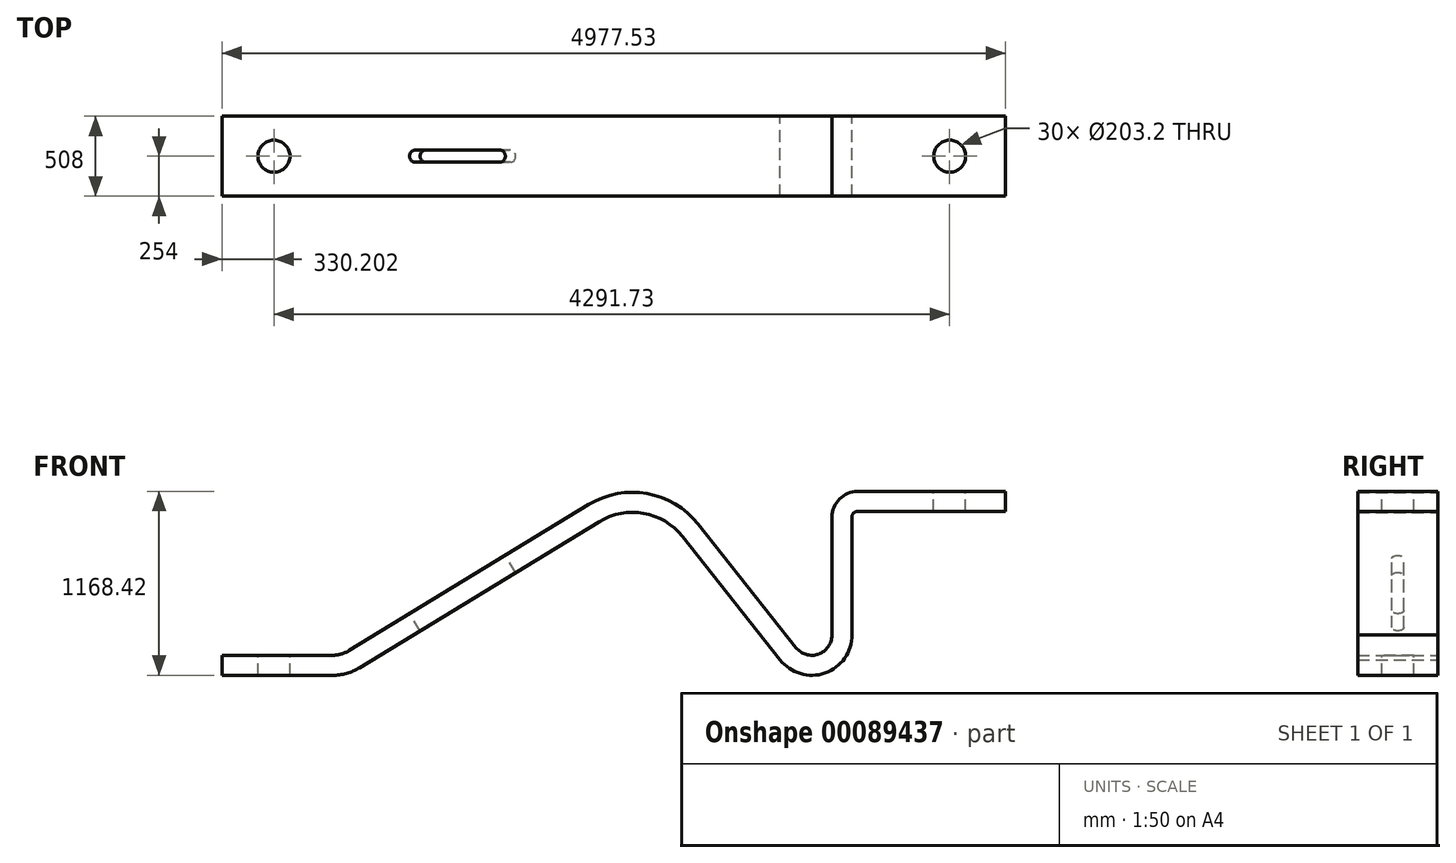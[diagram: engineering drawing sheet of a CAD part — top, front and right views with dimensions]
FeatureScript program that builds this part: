
annotation { "Feature Type Name" : "Feature", "Feature Type Description" : "" }
export const myFeature = defineFeature(function(context is Context, id is Id, definition is map)
    precondition{}
    {
        {
            var Q0;
            Q0=qCreatedBy(makeId("Front.planeOp"),FACE);
            var sketch = newSketch(context, id + "F0", { "sketchPlane" : qUnion([Q0])});
            skLineSegment(sketch, "E0", {"start": v(-1257.48, 129.45) * mm, "end": v(-555.68, 129.45) * mm});
            skLineSegment(sketch, "E1", {"start": v(-1257.48, 256.45) * mm, "end": v(-555.68, 256.45) * mm});
            skPoint(sketch, "E2", {"position": v(-555.68, 459.65) * mm});
            skArc(sketch, "E3", {"start": v(1071.43, 1213.55) * mm, "mid": v(1442.7, 1283.22) * mm, "end": v(1767, 1089.53) * mm});
            skLineSegment(sketch, "E4", {"start": v(-449.9, 286.15) * mm, "end": v(1071.43, 1213.55) * mm});
            skArc(sketch, "E5", {"start": v(1137.54, 1105.1) * mm, "mid": v(1420.4, 1158.2) * mm, "end": v(1667.5, 1010.62) * mm});
            skLineSegment(sketch, "E6", {"start": v(1667.5, 1010.62) * mm, "end": v(2290, 225.63) * mm});
            skArc(sketch, "E7", {"start": v(2389.51, 304.54) * mm, "mid": v(2530.8, 263.52) * mm, "end": v(2616.02, 383.45) * mm});
            skLineSegment(sketch, "E8", {"start": v(2831.05, 1297.85) * mm, "end": v(3720.05, 1297.85) * mm});
            skLineSegment(sketch, "E9", {"start": v(2781.12, 1170.85) * mm, "end": v(3720.05, 1170.85) * mm});
            skLineSegment(sketch, "E10", {"start": v(2831.05, 1297.85) * mm, "end": v(2781.12, 1297.85) * mm});
            skLineSegment(sketch, "E11", {"start": v(2743.02, 387.11) * mm, "end": v(2743.02, 1132.75) * mm});
            skArc(sketch, "E12", {"start": v(2781.12, 1170.85) * mm, "mid": v(2754.18, 1159.7) * mm, "end": v(2743.02, 1132.75) * mm});
            skArc(sketch, "E13", {"start": v(2781.12, 1297.85) * mm, "mid": v(2664.38, 1249.5) * mm, "end": v(2616.02, 1132.75) * mm});
            skLineSegment(sketch, "E14", {"start": v(3720.05, 1297.85) * mm, "end": v(3720.05, 1170.85) * mm});
            skLineSegment(sketch, "E15", {"start": v(-1257.48, 256.45) * mm, "end": v(-1257.48, 129.45) * mm});
            skArc(sketch, "E16", {"start": v(-555.68, 256.45) * mm, "mid": v(-500.75, 264.02) * mm, "end": v(-449.9, 286.15) * mm});
            skArc(sketch, "E17", {"start": v(-555.68, 129.45) * mm, "mid": v(-466.42, 141.74) * mm, "end": v(-383.8, 177.7) * mm});
            skLineSegment(sketch, "E18", {"start": v(2616.02, 1132.75) * mm, "end": v(2616.02, 383.45) * mm});
            skLineSegment(sketch, "E19", {"start": v(1767, 1089.53) * mm, "end": v(2389.51, 304.54) * mm});
            skLineSegment(sketch, "E20", {"start": v(-383.8, 177.7) * mm, "end": v(1137.54, 1105.1) * mm});
            skArc(sketch, "E21", {"start": v(2287.73, 228.5) * mm, "mid": v(2572.6, 143.57) * mm, "end": v(2743.02, 387.11) * mm});
            skSolve(sketch);
        }
        {
            var Q0;
            Q0 = qSketchRegion(id + "F0", true);
            extrude(context, id + "F1", {"entities" : qUnion([Q0]), "endBound" : BoundingType.SYMMETRIC, "depth" : 508 * mm});
        }
        {
            var Q0;
            Q0=makeQuery(id+"F1.opExtrude","SWEPT_FACE",FACE,{"disambiguationData":[OSD([sQuery(id+"F0.wireOp",EDGE,"E1")])]});
            var sketch = newSketch(context, id + "F2", { "sketchPlane" : qUnion([Q0])});
            skLineSegment(sketch, "E22", {"start": v(-1257.48, 0) * mm, "end": v(-927.28, 0) * mm, "construction": true});
            skPoint(sketch, "E22.endSnap0", {"position": v(-1257.48, 0) * mm});
            skCircle(sketch, "E23", {"center": v(-927.28, 0) * mm, "radius": 101.6 * mm});
            skPoint(sketch, "E24.0", {"position": v(3720.05, 0) * mm});
            skLineSegment(sketch, "E25", {"start": v(3720.05, 0) * mm, "end": v(3364.45, 0) * mm, "construction": true});
            skCircle(sketch, "E26", {"center": v(3364.45, 0) * mm, "radius": 101.6 * mm});
            skSolve(sketch);
        }
        {
            var Q0;
            Q0 = qSketchRegion(id + "F2", true);
            extrude(context, id + "F3", {"entities" : qUnion([Q0]), "operationType" : NewBodyOperationType.REMOVE, "endBound" : BoundingType.THROUGH_ALL, "oppositeDirection" : true, "depth" : 25.4 * mm});
        }
        {
            var Q0;
            Q0=makeQuery(id+"F1.opExtrude","SWEPT_FACE",FACE,{"disambiguationData":[OSD([sQuery(id+"F0.wireOp",EDGE,"E8"),sQuery(id+"F0.wireOp",EDGE,"E10")])]});
            var sketch = newSketch(context, id + "F4", { "sketchPlane" : qUnion([Q0])});
            skLineSegment(sketch, "E27", {"start": v(3720.05, 0) * mm, "end": v(3364.45, 0) * mm, "construction": true});
            skPoint(sketch, "E27.endSnap0", {"position": v(3720.05, 0) * mm});
            skCircle(sketch, "E28", {"center": v(3364.45, 0) * mm, "radius": 101.6 * mm});
            skSolve(sketch);
        }
        {
            var Q0;
            Q0 = qSketchRegion(id + "F4", true);
            extrude(context, id + "F5", {"entities" : qUnion([Q0]), "operationType" : NewBodyOperationType.REMOVE, "endBound" : BoundingType.THROUGH_ALL, "oppositeDirection" : true, "depth" : 25.4 * mm});
        }
        {
            var Q0;
            Q0=makeQuery(id+"F1.opExtrude","SWEPT_FACE",FACE,{"disambiguationData":[OSD([sQuery(id+"F0.wireOp",EDGE,"E4")])]});
            var sketch = newSketch(context, id + "F6", { "sketchPlane" : qUnion([Q0])});
            skPoint(sketch, "E29.0", {"position": v(-940.22, 0) * mm});
            skLineSegment(sketch, "E30", {"start": v(-940.22, 0) * mm, "end": v(-884.9, 0) * mm, "construction": true});
            skLineSegment(sketch, "E31", {"start": v(253.58, 38.1) * mm, "end": v(888.58, 38.1) * mm});
            skLineSegment(sketch, "E32", {"start": v(253.58, -38.1) * mm, "end": v(888.58, -38.1) * mm});
            skPoint(sketch, "E33.center.orphan", {"position": v(888.58, 0) * mm});
            skPoint(sketch, "E34.end.orphan", {"position": v(253.58, 0) * mm});
            skArc(sketch, "E35", {"start": v(253.58, 38.1) * mm, "mid": v(215.48, 0) * mm, "end": v(253.58, -38.1) * mm});
            skArc(sketch, "E36", {"start": v(888.58, -38.1) * mm, "mid": v(926.68, 0) * mm, "end": v(888.58, 38.1) * mm});
            skSolve(sketch);
        }
        {
            var Q0;
            Q0 = qSketchRegion(id + "F6", true);
            extrude(context, id + "F7", {"entities" : qUnion([Q0]), "operationType" : NewBodyOperationType.REMOVE, "endBound" : BoundingType.THROUGH_ALL, "oppositeDirection" : true, "depth" : 25.4 * mm});
        }
    });
